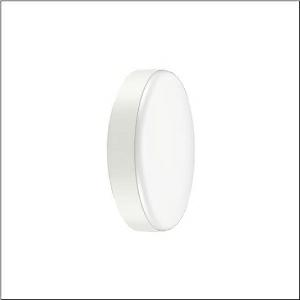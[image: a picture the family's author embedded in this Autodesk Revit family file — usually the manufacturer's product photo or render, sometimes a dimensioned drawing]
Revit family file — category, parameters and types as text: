
# Revit family: round_31_51wc10db34a
name_source: partatom
category: Lighting Fixtures
units: mm (PartAtom-declared; Revit-internal decimal feet)

## family parameters
Cut with Voids When Loaded = No
Host = Face
Light Source = No
Part Type = Normal
Room Calculation Point = No
Round Connector Dimension = Use Diameter
Shared = No

## types (1)
- Round 31 (1 x LED, 4250 lm, 34 W, 3000K)
    Apparent Load = 34 VA
    CIE Flux Codes = 44 75 94 94 100
    Color Rendering = 80
    Color Temperature = 3000K
    Default Elevation = 1800 mm
    Description = Round 31, wall and ceiling luminaire, primary optical cover: cover, of PC, opal, light emission: direct distribution, primary light characteristic: symmetric, installation type: surface-mounted, LED, rated luminous flux: 4.250lm, luminous efficacy: 125lm/W, light colour: 830, colour temperature: 3000K, control gear: DALI 2, with terminal, 5-pole, max. 2.5mm², mains connection: 220..240V, AC, 50/60Hz, rated input power: 34W, luminaire housing, of PC, traffic white (RAL 9016), diameter: 480mm, protection rating (complete): IP65, insulation class (complete): insulation class II (safety insulation), certification: CE, impact resistance: IK10, permissible operating ambient temperature: -20..+40°C, permissible storage temperature: -20..+60°C, packaging unit: 1 piece
    Height = 97 mm
    Lamp = 1 x LED
    Lamp Light Flux = 4250 lm
    Lamp Power = 34 W
    Lamp count = 1
    Length = 480 mm
    Luminous efficacy = 125 lm/W
    Manufacturer = Siteco
    ModVariant = No
    Model = 51WC10DB34A
    Mounting Place = Ceiling
    Mounting Type = Surface mounted
    Number of Poles = 1
    OnlyDefault = Yes
    Power Factor = 1
    Product Name = Round 31
    Product group = wall and ceiling luminaire
    ProductGroupID = 304
    Protection Class = Protection class II
    Protection Degree = IP 65
    RLX_Detail_Level = 1
    RLX_Emergency_Light_Flux = 0 lm
    RLX_Emergency_Type = 0
    RLX_Emergency_Type_DB = No
    RlxData = <blob elided: 55341 chars, md5=4955ac63>
    Socket = socket
    Standby Power = 0 W
    System Light Flux = 4250 lm
    System Power = 34 W
    Type Comments = Product without accessories
    Type Image = l_1007188.jpg
    URL = http://relux.com
    VarID = ---
    Voltage = 0 V
    Weight = 0.00 kg
    Width = 0 mm  [stored 0 ft]

note: [stored X ft] marks values corroborated as IEEE doubles in the binary element streams (Revit-internal decimal feet)

## geometry (parser evidence)
native form markers: Blend x4, Sweep x12
no freeform markers — native parametric forms only
